# Revit family: 59-P-I
name_source: partatom
category: Lighting Fixtures
revit_build: Autodesk Revit 2013 (Build: 20130531_2115(x64)
units: mm (PartAtom-declared; Revit-internal decimal feet)

## types (2) — shared parameters
Apparent Load = 123 VA
Assembly Code = D5020210
Color Filter = 16777215
Default Elevation = 48.0"
Description = Arcos Pendant Indirect
Dimming Lamp Color Temperature Shift = <None>
Emit Shape Visible in Rendering = No
Emit from Rectangle Length = 8.0"
Emit from Rectangle Width = 42.0"
Glass = Hubbell-White Glass
Lamp = LED Lamp
Load Classification = Lighting
Manufacturer = Alera Lighting
Manufacturer Fax = 866-898-1065
Model = 59-P-I
Mounting = Pendant
Nominal Watts = 123 W
Photometric Notes = More IES files download Photometric Web Link
Photometric Web File = 59-P-I-04-SGL-Cx-2T5HO.ies
Photometric Web Link = http://www.hubbelllighting.com
Power Factor = 1
Product Documentation Link = http://cdn.litecontrol.com
Product Page URL = http://www.litecontrol.com
URL = http://www.aleralighting.com
Voltage = 120 V

## per-type parameters (varying)
| type | Backbox | Tilt Angle |
| 59-P-I-Camera Black | Hubbell-Camera Black | -90.00° |
| 59-P-I-Matte White | Hubbell-Matte White | 90.00° |

## geometry (parser evidence)
native form markers: Blend x4, Sweep x3
no freeform markers — native parametric forms only
